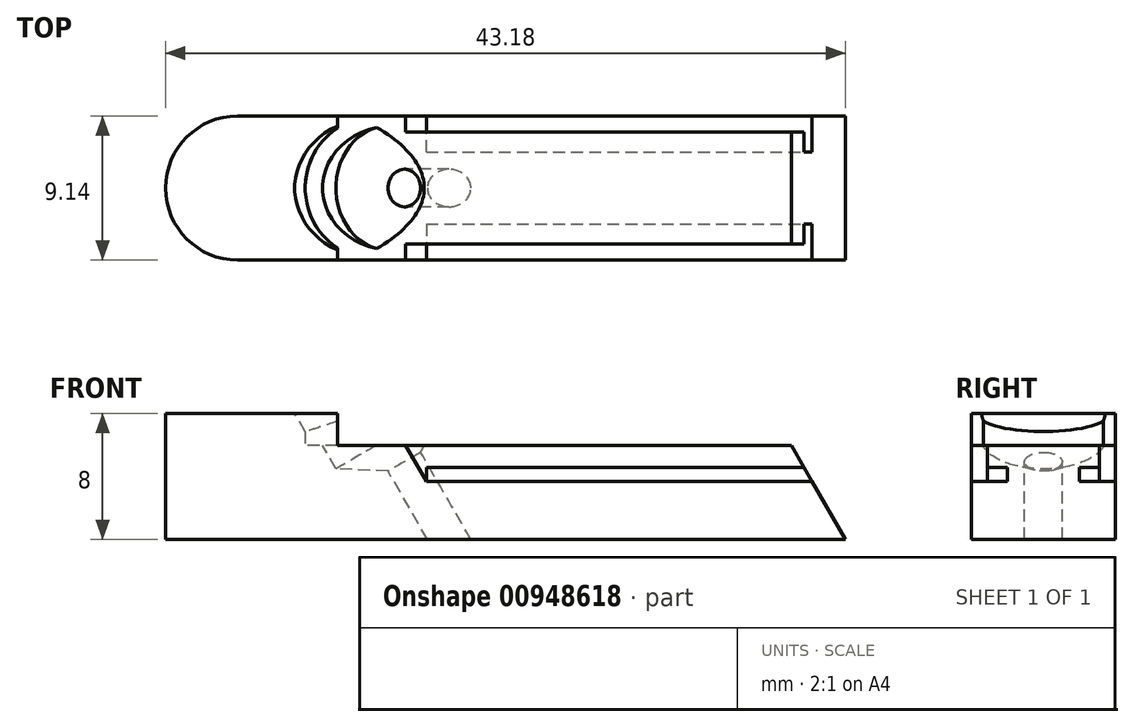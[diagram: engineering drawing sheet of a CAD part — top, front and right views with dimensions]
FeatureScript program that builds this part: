
annotation { "Feature Type Name" : "Feature", "Feature Type Description" : "" }
export const myFeature = defineFeature(function(context is Context, id is Id, definition is map)
    precondition{}
    {
        {
            var Q0;
            Q0=qCreatedBy(makeId("Top.planeOp"),FACE);
            var sketch = newSketch(context, id + "F0", { "sketchPlane" : qUnion([Q0])});
            skLineSegment(sketch, "E0", {"start": v(-13.44, 4.57) * mm, "end": v(25.17, 4.57) * mm});
            skLineSegment(sketch, "E1", {"start": v(25.17, 4.57) * mm, "end": v(25.17, -4.57) * mm});
            skLineSegment(sketch, "E2", {"start": v(25.17, -4.57) * mm, "end": v(-13.44, -4.57) * mm});
            skArc(sketch, "E3", {"start": v(-13.44, 4.57) * mm, "mid": v(-18, 0) * mm, "end": v(-13.44, -4.57) * mm});
            skSolve(sketch);
        }
        {
            var Q0;
            Q0=makeQuery(id+"F0.imprint","IMPRINT",FACE,{"disambiguationData":[TD([[makeQuery(id+"F0.imprint","IMPRINT",EDGE,{"derivedFrom":sQuery(id+"F0.wireOp",EDGE,"E0")}),-1.0]])]});
            extrude(context, id + "F1", {"entities" : qUnion([Q0]), "depth" : 5.97 * mm, "offsetDistance" : 25.4 * mm});
        }
        {
            var Q0;
            Q0=makeQuery(id+"F1.opExtrude","SWEPT_FACE",FACE,{"disambiguationData":[OSD([sQuery(id+"F0.wireOp",EDGE,"E2")])]});
            var sketch = newSketch(context, id + "F2", { "sketchPlane" : qUnion([Q0])});
            skLineSegment(sketch, "E4", {"start": v(-1.45, 3.68) * mm, "end": v(25.17, 3.68) * mm});
            skLineSegment(sketch, "E5", {"start": v(25.17, 3.68) * mm, "end": v(25.17, 5.97) * mm});
            skLineSegment(sketch, "E6", {"start": v(25.17, 5.97) * mm, "end": v(-2.77, 5.97) * mm});
            skLineSegment(sketch, "E7", {"start": v(-2.77, 5.97) * mm, "end": v(-1.45, 3.68) * mm});
            skSolve(sketch);
        }
        {
            var Q0;
            Q0 = qSketchRegion(id + "F2", true);
            extrude(context, id + "F3", {"entities" : qUnion([Q0]), "operationType" : NewBodyOperationType.REMOVE, "oppositeDirection" : true, "depth" : 1.02 * mm, "offsetDistance" : 25.4 * mm});
        }
        {
            var Q0;
            Q0=makeQuery(id+"F3.boolean.opBoolean","COPY",FACE,{"derivedFrom":makeQuery(id+"F3.opExtrude","CAP_FACE",FACE,{"disambiguationData":[OSD([sQuery(id+"F2.wireOp",EDGE,"E4"),sQuery(id+"F2.wireOp",EDGE,"E5"),sQuery(id+"F2.wireOp",EDGE,"E6"),sQuery(id+"F2.wireOp",EDGE,"E7")])],"isStart":false})});
            var sketch = newSketch(context, id + "F4", { "sketchPlane" : qUnion([Q0])});
            skLineSegment(sketch, "E8.bottom", {"start": v(-1.45, 3.68) * mm, "end": v(25.17, 3.68) * mm});
            skLineSegment(sketch, "E8.top", {"start": v(-1.45, 4.57) * mm, "end": v(25.17, 4.57) * mm});
            skLineSegment(sketch, "E8.left", {"start": v(-1.45, 3.68) * mm, "end": v(-1.45, 4.57) * mm});
            skLineSegment(sketch, "E8.right", {"start": v(25.17, 3.68) * mm, "end": v(25.17, 4.57) * mm});
            skSolve(sketch);
        }
        {
            var Q0;
            Q0 = qSketchRegion(id + "F4", true);
            extrude(context, id + "F5", {"entities" : qUnion([Q0]), "operationType" : NewBodyOperationType.REMOVE, "oppositeDirection" : true, "depth" : 1.27 * mm, "offsetDistance" : 25.4 * mm});
        }
        {
            var Q0;
            Q0=makeQuery(id+"F1.opExtrude","SWEPT_FACE",FACE,{"disambiguationData":[OSD([sQuery(id+"F0.wireOp",EDGE,"E2")])]});
            var sketch = newSketch(context, id + "F6", { "sketchPlane" : qUnion([Q0])});
            skLineSegment(sketch, "E9", {"start": v(25.17, 0) * mm, "end": v(25.17, 5.97) * mm});
            skLineSegment(sketch, "E10", {"start": v(25.17, 5.97) * mm, "end": v(21.73, 5.97) * mm});
            skLineSegment(sketch, "E11", {"start": v(21.73, 5.97) * mm, "end": v(25.17, 0) * mm});
            skSolve(sketch);
        }
        {
            var Q0;
            Q0 = qSketchRegion(id + "F6", true);
            extrude(context, id + "F7", {"entities" : qUnion([Q0]), "operationType" : NewBodyOperationType.REMOVE, "endBound" : BoundingType.THROUGH_ALL, "oppositeDirection" : true, "depth" : 25.4 * mm, "offsetDistance" : 25.4 * mm});
        }
        {
            var Q0;
            Q0=makeQuery(id+"F1.opExtrude","SWEPT_BODY",BODY,{"disambiguationData":[OSD([sQuery(id+"F0.wireOp",EDGE,"E0"),sQuery(id+"F0.wireOp",EDGE,"E1"),sQuery(id+"F0.wireOp",EDGE,"E2"),sQuery(id+"F0.wireOp",EDGE,"E3")])]});
            var Q1;
            Q1=qCreatedBy(makeId("Front.planeOp"),FACE);
            mirror(context, id + "F8", {"operationType" : NewBodyOperationType.INTERSECT, "entities" : qUnion([Q0]), "mirrorPlane" : qUnion([Q1])});
        }
        {
            var Q0;
            Q0=makeQuery(id+"F1.opExtrude","CAP_FACE",FACE,{"disambiguationData":[OSD([sQuery(id+"F0.wireOp",EDGE,"E0"),sQuery(id+"F0.wireOp",EDGE,"E1"),sQuery(id+"F0.wireOp",EDGE,"E2"),sQuery(id+"F0.wireOp",EDGE,"E3")])],"isStart":false});
            var sketch = newSketch(context, id + "F9", { "sketchPlane" : qUnion([Q0])});
            skArc(sketch, "E12", {"start": v(-13.44, 4.57) * mm, "mid": v(-18, 0) * mm, "end": v(-13.44, -4.57) * mm});
            skLineSegment(sketch, "E13", {"start": v(-13.44, 4.57) * mm, "end": v(-7.1, 4.57) * mm});
            skLineSegment(sketch, "E14", {"start": v(-13.44, -4.57) * mm, "end": v(-7.1, -4.57) * mm});
            skLineSegment(sketch, "E15", {"start": v(-13.44, 4.57) * mm, "end": v(-13.44, -4.57) * mm, "construction": true});
            skLineSegment(sketch, "E16", {"start": v(-7.1, 4.57) * mm, "end": v(-7.1, 3.81) * mm});
            skArc(sketch, "E17", {"start": v(-7.1, 3.81) * mm, "mid": v(-9.14, 0) * mm, "end": v(-7.1, -3.81) * mm});
            skLineSegment(sketch, "E18", {"start": v(-7.1, -3.81) * mm, "end": v(-7.1, -3.81) * mm});
            skLineSegment(sketch, "E19", {"start": v(-7.1, -3.81) * mm, "end": v(-7.1, -4.57) * mm});
            skSolve(sketch);
        }
        {
            var Q0;
            Q0 = qSketchRegion(id + "F9", true);
            extrude(context, id + "F10", {"entities" : qUnion([Q0]), "operationType" : NewBodyOperationType.ADD, "depth" : 2.03 * mm, "offsetDistance" : 25.4 * mm});
        }
        {
            var Q0;
            Q0=qCreatedBy(makeId("Front.planeOp"),FACE);
            var sketch = newSketch(context, id + "F11", { "sketchPlane" : qUnion([Q0])});
            skLineSegment(sketch, "E20", {"start": v(0, 0) * mm, "end": v(-7.37, 12.76) * mm});
            skLineSegment(sketch, "E21", {"start": v(-7.2, 4.48) * mm, "end": v(-3.88, 4.34) * mm});
            skLineSegment(sketch, "E22", {"start": v(-3.88, 4.34) * mm, "end": v(0.87, -3.9) * mm});
            skLineSegment(sketch, "E23", {"start": v(0.87, -3.9) * mm, "end": v(1.9, -3.3) * mm});
            skLineSegment(sketch, "E24", {"start": v(1.9, -3.3) * mm, "end": v(0, 0) * mm});
            skLineSegment(sketch, "E25", {"start": v(-8.05, 5.97) * mm, "end": v(-7.2, 4.48) * mm});
            skLineSegment(sketch, "E26", {"start": v(-8.05, 5.97) * mm, "end": v(-8.64, 5.97) * mm});
            skLineSegment(sketch, "E27", {"start": v(-8.64, 5.97) * mm, "end": v(-11.26, 10.51) * mm});
            skLineSegment(sketch, "E28", {"start": v(-7.37, 12.76) * mm, "end": v(-11.26, 10.51) * mm});
            skSolve(sketch);
        }
        {
            var Q0;
            Q0 = qSketchRegion(id + "F11", true);
            var Q1;
            Q1=sQuery(id+"F11.wireOp",EDGE,"E20");
            revolve(context, id + "F12", {"operationType" : NewBodyOperationType.REMOVE, "surfaceOperationType" : NewSurfaceOperationType.NEW, "entities" : qUnion([Q0]), "axis" : qUnion([Q1]), "revolveType" : RevolveType.FULL, "oppositeDirection" : true});
        }
    });
